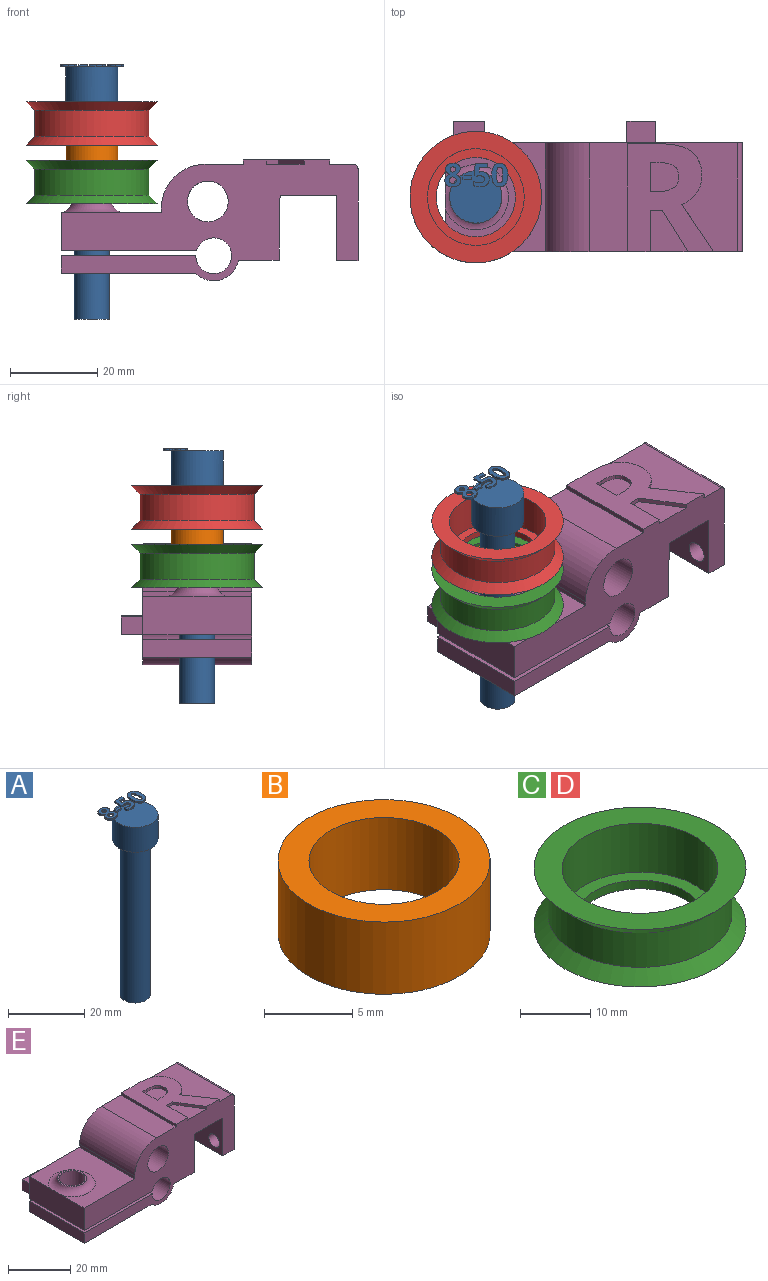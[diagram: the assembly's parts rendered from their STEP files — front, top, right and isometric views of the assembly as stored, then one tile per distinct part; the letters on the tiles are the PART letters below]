
ASSEMBLY  parts=5 mates=4
PART A: 86 faces, bbox 14.5x13.7x58.5 mm
  f0: plane 12x12mm, normal (0,0,1), area 99.4mm2, adj f5,f22,f23,f24,f25,f26,f40,f41
  f1: plane 1x0.26mm, normal (0,0,1), area 0.1mm2, adj f5,f46,f47,f48,f49
  f2: plane 0.85x0.68mm, normal (0,0,1), area 0.2mm2, adj f5,f29,f30,f31
  f3: cylinder r=4mm len=50mm, axis (0,0,-1), area 1256.6mm2, adj f4,f6
  f4: plane 8x8mm, normal (0,0,-1), area 50.3mm2, adj f3
  f5: cylinder r=6mm len=12mm, axis (0,0,-1), area 301.6mm2, adj f0,f1,f2,f6,f39,f45,f67,f85
  f6: plane 12x12mm, normal (0,0,-1), area 62.8mm2, adj f3,f5
  f7: extruded ~0.5x0.46mm, area 0.2mm2, adj f8,f37,f38,f39
  f8: extruded ~0.5x0.46mm, area 0.2mm2, adj f7,f9,f38,f39
  f9: extruded ~0.5x0.39mm, area 0.2mm2, adj f8,f10,f38,f39
  f10: extruded ~0.5x0.4mm, area 0.2mm2, adj f9,f11,f38,f39
  f11: extruded ~0.5x0.49mm, area 0.3mm2, adj f10,f12,f38,f39
  f12: extruded ~0.5x0.5mm, area 0.3mm2, adj f11,f13,f38,f39
  f13: extruded ~0.5x0.39mm, area 0.2mm2, adj f12,f37,f38,f39
  f14: extruded ~1.22x0.5mm, area 0.6mm2, adj f15,f35,f38,f39
  f15: extruded ~1.22x0.5mm, area 0.6mm2, adj f14,f16,f38,f39
  f16: extruded ~0.91x0.5mm, area 0.5mm2, adj f15,f17,f38,f39
  f17: extruded ~0.71x0.5mm, area 0.4mm2, adj f16,f18,f38,f39
  f18: extruded ~0.65x0.61mm, area 0.4mm2, adj f17,f19,f38,f39
  f19: extruded ~0.77x0.62mm, area 0.5mm2, adj f18,f20,f38,f39
  f20: extruded ~0.8x0.5mm, area 0.4mm2, adj f19,f21,f38,f39
  f21: extruded ~1.04x0.5mm, area 0.6mm2, adj f20,f22,f38,f39
  f22: extruded ~1.36x0.5mm, area 0.7mm2, adj f0,f21,f23,f38,f39
  f23: extruded ~1.33x0.5mm, area 0.7mm2, adj f0,f22,f24,f38
  f24: extruded ~1.04x0.51mm, area 0.6mm2, adj f0,f23,f25,f38
  f25: extruded ~0.75x0.5mm, area 0.4mm2, adj f0,f24,f26,f38
  f26: extruded ~0.85x0.66mm, area 0.5mm2, adj f0,f25,f27,f38,f39
  f27: extruded ~0.72x0.56mm, area 0.5mm2, adj f26,f28,f38,f39
  f28: extruded ~0.72x0.5mm, area 0.4mm2, adj f27,f35,f38,f39
  f29: extruded ~0.5x0.45mm, area 0.3mm2, adj f2,f30,f36,f38,f39
  f30: extruded ~0.5x0.47mm, area 0.3mm2, adj f2,f29,f31,f38
  f31: extruded ~0.62x0.5mm, area 0.3mm2, adj f2,f30,f32,f38,f39
  f32: extruded ~0.59x0.5mm, area 0.3mm2, adj f31,f33,f38,f39
  f33: extruded ~0.5x0.48mm, area 0.3mm2, adj f32,f34,f38,f39
  f34: extruded ~0.89x0.77mm, area 0.6mm2, adj f33,f36,f38,f39
  f35: extruded ~0.93x0.5mm, area 0.5mm2, adj f14,f28,f38,f39
  f36: extruded ~0.66x0.5mm, area 0.4mm2, adj f29,f34,f38,f39
  f37: extruded ~0.5x0.39mm, area 0.2mm2, adj f7,f13,f38,f39
  f38: plane 5.4x3.69mm, normal (0,0,1), area 12.7mm2, adj f7,f8,f9,f10,f11,f12,f13,f14
  f39: plane 5.4x3.53mm, normal (0,0,-1), area 10.2mm2, adj f5,f7,f8,f9,f10,f11,f12,f13
  f40: plane 0.9x0.5mm, normal (-1,0,0), area 0.4mm2, adj f0,f41,f43,f44
  f41: plane 1.93x0.5mm, normal (0,-1,0), area 1mm2, adj f0,f40,f42,f44
  f42: plane 0.9x0.5mm, normal (1,0,0), area 0.4mm2, adj f0,f41,f43,f44
  f43: plane 1.93x0.5mm, normal (0,1,0), area 1mm2, adj f0,f40,f42,f44
  f44: plane 1.93x0.9mm, normal (0,0,1), area 1.7mm2, adj f40,f41,f42,f43
  f45: plane 0.76x0.31mm, normal (0,0,-1), area 0mm2, adj f5,f46
  f46: extruded ~1.21x0.5mm, area 0.7mm2, adj f0,f1,f45,f47,f65,f66
  f47: extruded ~0.54x0.5mm, area 0.3mm2, adj f1,f46,f48,f66
  f48: plane 0.5x0.13mm, normal (-0.2,0.98,0), area 0.1mm2, adj f1,f47,f49,f66
  f49: plane 1.03x0.5mm, normal (1,-0.09,0), area 0.5mm2, adj f1,f48,f50,f66,f67
  f50: plane 1.88x0.5mm, normal (0,-1,0), area 0.9mm2, adj f49,f51,f66,f67
  f51: plane 0.94x0.5mm, normal (1,0,0), area 0.5mm2, adj f50,f52,f66,f67
  f52: plane 2.85x0.5mm, normal (0,1,0), area 1.4mm2, adj f51,f53,f66,f67
  f53: plane 2.68x0.5mm, normal (-1,0.07,0), area 1.3mm2, adj f0,f52,f54,f66,f67
  f54: plane 0.5x0.44mm, normal (-0.47,-0.88,0), area 0.3mm2, adj f0,f53,f55,f66
  f55: extruded ~0.5x0.37mm, area 0.2mm2, adj f0,f54,f56,f66
  f56: extruded ~0.5x0.42mm, area 0.2mm2, adj f0,f55,f57,f66
  f57: extruded ~1.05x0.8mm, area 0.8mm2, adj f0,f56,f58,f66
  f58: extruded ~1.02x0.83mm, area 0.8mm2, adj f0,f57,f59,f66
  f59: extruded ~0.72x0.5mm, area 0.4mm2, adj f0,f58,f60,f66
  f60: extruded ~0.66x0.5mm, area 0.4mm2, adj f0,f59,f61,f66
  f61: plane 0.96x0.5mm, normal (-1,0,0), area 0.5mm2, adj f0,f60,f62,f66
  f62: extruded ~1.42x0.5mm, area 0.7mm2, adj f0,f61,f63,f66
  f63: extruded ~1.55x0.5mm, area 0.8mm2, adj f0,f62,f64,f66
  f64: extruded ~1.36x0.54mm, area 0.8mm2, adj f0,f63,f65,f66
  f65: extruded ~1.17x0.5mm, area 0.6mm2, adj f0,f46,f64,f66
  f66: plane 5.33x3.51mm, normal (0,0,1), area 10.9mm2, adj f46,f47,f48,f49,f50,f51,f52,f53
  f67: plane 2.97x1.71mm, normal (0,0,-1), area 3.5mm2, adj f5,f49,f50,f51,f52,f53
  f68: extruded ~1.39x0.5mm, area 0.7mm2, adj f69,f83,f84,f85
  f69: extruded ~1.39x0.5mm, area 0.7mm2, adj f68,f70,f84,f85
  f70: extruded ~0.56x0.5mm, area 0.4mm2, adj f69,f71,f84,f85
  f71: extruded ~0.56x0.5mm, area 0.4mm2, adj f70,f72,f84,f85
  f72: extruded ~1.39x0.5mm, area 0.7mm2, adj f71,f73,f84,f85
  f73: extruded ~1.38x0.5mm, area 0.7mm2, adj f72,f74,f84,f85
  f74: extruded ~0.56x0.5mm, area 0.4mm2, adj f73,f83,f84,f85
  f75: extruded ~2.04x0.5mm, area 1.1mm2, adj f76,f82,f84,f85
  f76: extruded ~2.02x0.5mm, area 1.1mm2, adj f75,f77,f84,f85
  f77: extruded ~1.38x0.69mm, area 0.8mm2, adj f76,f78,f84,f85
  f78: extruded ~1.38x0.66mm, area 0.8mm2, adj f77,f79,f84,f85
  f79: extruded ~2.05x0.5mm, area 1.1mm2, adj f78,f80,f84,f85
  f80: extruded ~2.02x0.5mm, area 1mm2, adj f0,f79,f81,f84,f85
  f81: extruded ~1.37x0.68mm, area 0.8mm2, adj f0,f80,f82,f84
  f82: extruded ~1.39x0.66mm, area 0.8mm2, adj f0,f75,f81,f84,f85
  f83: extruded ~0.56x0.5mm, area 0.4mm2, adj f68,f74,f84,f85
  f84: plane 5.41x3.68mm, normal (0,0,1), area 12.1mm2, adj f68,f69,f70,f71,f72,f73,f74,f75
  f85: plane 5.41x3.68mm, normal (0,0,-1), area 10.3mm2, adj f5,f68,f69,f70,f71,f72,f73,f74
PART B: 4 faces, bbox 12x12x5 mm
  f0: cylinder r=4.25mm len=8.5mm, axis (0,0,-1), area 133.5mm2, adj f2,f3
  f1: cylinder r=6mm len=12mm, axis (0,0,-1), area 188.5mm2, adj f2,f3
  f2: plane 12x12mm, normal (0,0,1), area 56.4mm2, adj f0,f1
  f3: plane 12x12mm, normal (0,0,-1), area 56.4mm2, adj f0,f1
PART C: 8 faces, bbox 30.2x30.2x10 mm
  f0: plane 30.2x30.2mm, normal (0,0,1), area 329.2mm2, adj f1,f7
  f1: cylinder r=11.1mm len=22.2mm, axis (0,0,-1), area 592.8mm2, adj f0,f2
  f2: plane 22.2x22.2mm, normal (0,0,1), area 126.9mm2, adj f1,f3
  f3: cylinder r=9.1mm len=18.2mm, axis (0,0,-1), area 85.8mm2, adj f2,f4
  f4: plane 30.2x30.2mm, normal (0,0,-1), area 456.2mm2, adj f3,f5
  f5: cone r=13.1mm half-angle=45deg, axis (0,0,-1), area 250.6mm2, adj f4,f6
  f6: cylinder r=13.1mm len=26.2mm, axis (0,0,-1), area 493.9mm2, adj f5,f7
  f7: cone r=15.1mm half-angle=45deg, axis (0,0,1), area 250.6mm2, adj f0,f6
PART D: same geometry as C
PART E: 56 faces, bbox 71.6x30x27.7 mm
  f0: plane 34.12x25mm, normal (0,0,1), area 459.6mm2, adj f14,f15,f25,f27,f40,f41,f42,f43
  f1: plane 9.51x8.71mm, normal (0,0,1), area 54.7mm2, adj f14,f37,f38,f39
  f2: plane 25x4.12mm, normal (-1,0,0), area 103mm2, adj f5,f14,f15,f19
  f3: cylinder r=4.17mm len=8.35mm, axis (0,0,1), area 108.1mm2, adj f5,f19
  f4: plane 25x9.34mm, normal (0,0,-1), area 233.4mm2, adj f13,f14,f15,f17
  f5: plane 30.88x25mm, normal (0,0,-1), area 717.2mm2, adj f2,f3,f14,f15,f17
  f6: plane 25x8.82mm, normal (-1,0,0), area 219.6mm2, adj f7,f14,f15,f20,f24
  f7: plane 25x23mm, normal (0,0,1), area 400mm2, adj f6,f8,f14,f15,f24
  f8: plane 25x1.1mm, normal (-1,0,0), area 27.5mm2, adj f7,f14,f15,f25
  f9: plane 25x21.09mm, normal (1,0,0), area 493.5mm2, adj f10,f14,f15,f22,f23,f27
  f10: plane 25x5mm, normal (0,0,-1), area 125mm2, adj f9,f11,f14,f15
  f11: plane 25x15mm, normal (-1,0,0), area 341.3mm2, adj f10,f12,f14,f15,f22,f23
  f12: plane 25x12.9mm, normal (0,0,-1), area 322.5mm2, adj f11,f13,f14,f15
  f13: plane 25x14.91mm, normal (1,0,-0.01), area 372.8mm2, adj f4,f12,f14,f15
  f14: plane 68.12x27.75mm, normal (0,-1,0), area 1017mm2, adj f0,f1,f2,f4,f5,f6,f7,f8
  f15: plane 68.12x26.75mm, normal (0,1,0), area 945.9mm2, adj f0,f2,f4,f5,f6,f7,f8,f9
  f16: cylinder r=4.17mm len=10.78mm, axis (0,0,1), area 282.8mm2, adj f20,f21
  f17: cylinder r=5.75mm len=25mm, axis (0,-1,0), area 315.9mm2, adj f4,f5,f14,f15
  f18: cylinder r=4.1mm len=25mm, axis (0,-1,0), area 618.7mm2, adj f14,f15,f19,f20
  f19: plane 30.91x25mm, normal (0,0,1), area 718.1mm2, adj f2,f3,f14,f15,f18
  f20: plane 31.07x30mm, normal (0,0,-1), area 758.4mm2, adj f6,f14,f15,f16,f18,f29,f30,f31
  f21: plane 9.35x9.35mm, normal (0,0,1), area 13.9mm2, adj f16,f24
  f22: cylinder r=2.43mm len=5mm, axis (1,0,0), area 76.2mm2, adj f9,f11
  f23: cylinder r=2.2mm len=5mm, axis (1,0,0), area 69.1mm2, adj f9,f11
  f24: torus R=7.5mm, axis (0,0,-1), area 134.6mm2, adj f6,f7,f21
  f25: cylinder r=10mm len=25mm, axis (0,-1,0), area 392.7mm2, adj f0,f8,f14,f15
  f26: cylinder r=4.68mm len=25mm, axis (0,-1,0), area 735.2mm2, adj f14,f15
  f27: cylinder r=1mm len=25mm, axis (0,-1,0), area 39.3mm2, adj f0,f9,f14,f15
  f28: plane 7.3x5mm, normal (0,0,1), area 36.5mm2, adj f15,f29,f30,f31
  f29: plane 5x4.12mm, normal (-1,0,0), area 20.6mm2, adj f15,f20,f28,f31
  f30: plane 5x4.12mm, normal (1,0,0), area 20.6mm2, adj f15,f20,f28,f31
  f31: plane 7.3x4.12mm, normal (0,1,0), area 30.1mm2, adj f20,f28,f29,f30
  f32: plane 6.63x5mm, normal (0,0,1), area 33.2mm2, adj f15,f33,f35,f36
  f33: plane 5x4.5mm, normal (-1,0,0), area 22.5mm2, adj f15,f32,f34,f36
  f34: plane 6.63x5mm, normal (0,0,-1), area 33.2mm2, adj f15,f33,f35,f36
  f35: plane 5x4.5mm, normal (1,0,0), area 22.5mm2, adj f15,f32,f34,f36
  f36: plane 6.63x4.5mm, normal (0,1,0), area 29.9mm2, adj f32,f33,f34,f35
  f37: plane 9.51x1mm, normal (1,0,0), area 9.5mm2, adj f1,f14,f38,f54
  f38: plane 2.79x1mm, normal (0,-1,0), area 2.8mm2, adj f1,f37,f39,f54
  f39: plane 9.51x5.92mm, normal (-0.85,-0.53,0), area 11.2mm2, adj f1,f14,f38,f54
  f40: extruded ~10.8x7.29mm, area 13mm2, adj f0,f14,f41,f54
  f41: extruded ~3.41x2.67mm, area 4.4mm2, adj f0,f40,f42,f54
  f42: extruded ~3.89x1.2mm, area 4.1mm2, adj f0,f41,f43,f54
  f43: extruded ~5.59x2.42mm, area 6.3mm2, adj f0,f42,f44,f54
  f44: extruded ~7.48x1.84mm, area 7.8mm2, adj f0,f43,f45,f54
  f45: plane 7.22x1mm, normal (0,1,0), area 7.2mm2, adj f0,f44,f46,f54
  f46: plane 24.79x1mm, normal (-1,0,0), area 24.8mm2, adj f0,f14,f45,f54
  f47: plane 1.69x1mm, normal (0,1,0), area 1.7mm2, adj f48,f53,f54,f55
  f48: plane 6.7x1mm, normal (1,0,0), area 6.7mm2, adj f47,f49,f54,f55
  f49: plane 1.6x1mm, normal (0,-1,0), area 1.6mm2, adj f48,f50,f54,f55
  f50: extruded ~3.75x1mm, area 3.9mm2, adj f49,f51,f54,f55
  f51: extruded ~2.51x1.21mm, area 2.9mm2, adj f50,f52,f54,f55
  f52: extruded ~2.61x1.19mm, area 3mm2, adj f51,f53,f54,f55
  f53: extruded ~3.68x1mm, area 3.8mm2, adj f47,f52,f54,f55
  f54: plane 24.79x19.8mm, normal (0,0,1), area 300mm2, adj f14,f37,f38,f39,f40,f41,f42,f43
  f55: plane 6.7x6.56mm, normal (0,0,1), area 38.8mm2, adj f47,f48,f49,f50,f51,f52,f53
PLACE A t=(-103.78,-12.5,-13.6)mm
PLACE B rot(axis=(1,0,0),180deg) t=(-103.78,-12.5,26.4)mm
PLACE C t=(-103.78,-12.5,18.1)mm
PLACE D t=(-103.78,-12.5,31.6)mm
PLACE E at identity
MATE fastened A.f3 <-> D.f1  axis (0,0,-1) through (-103.78,-12.5,36.4)mm
MATE fastened B.f0 <-> C.f1  axis (0,0,1) through (-103.78,-12.5,21.4)mm
MATE fastened C.f1 <-> E.f3  axis (0,0,-1) through (-103.78,-12.5,12.9)mm
MATE fastened D.f1 <-> B.f0  axis (0,0,-1) through (-103.78,-12.5,26.4)mm
